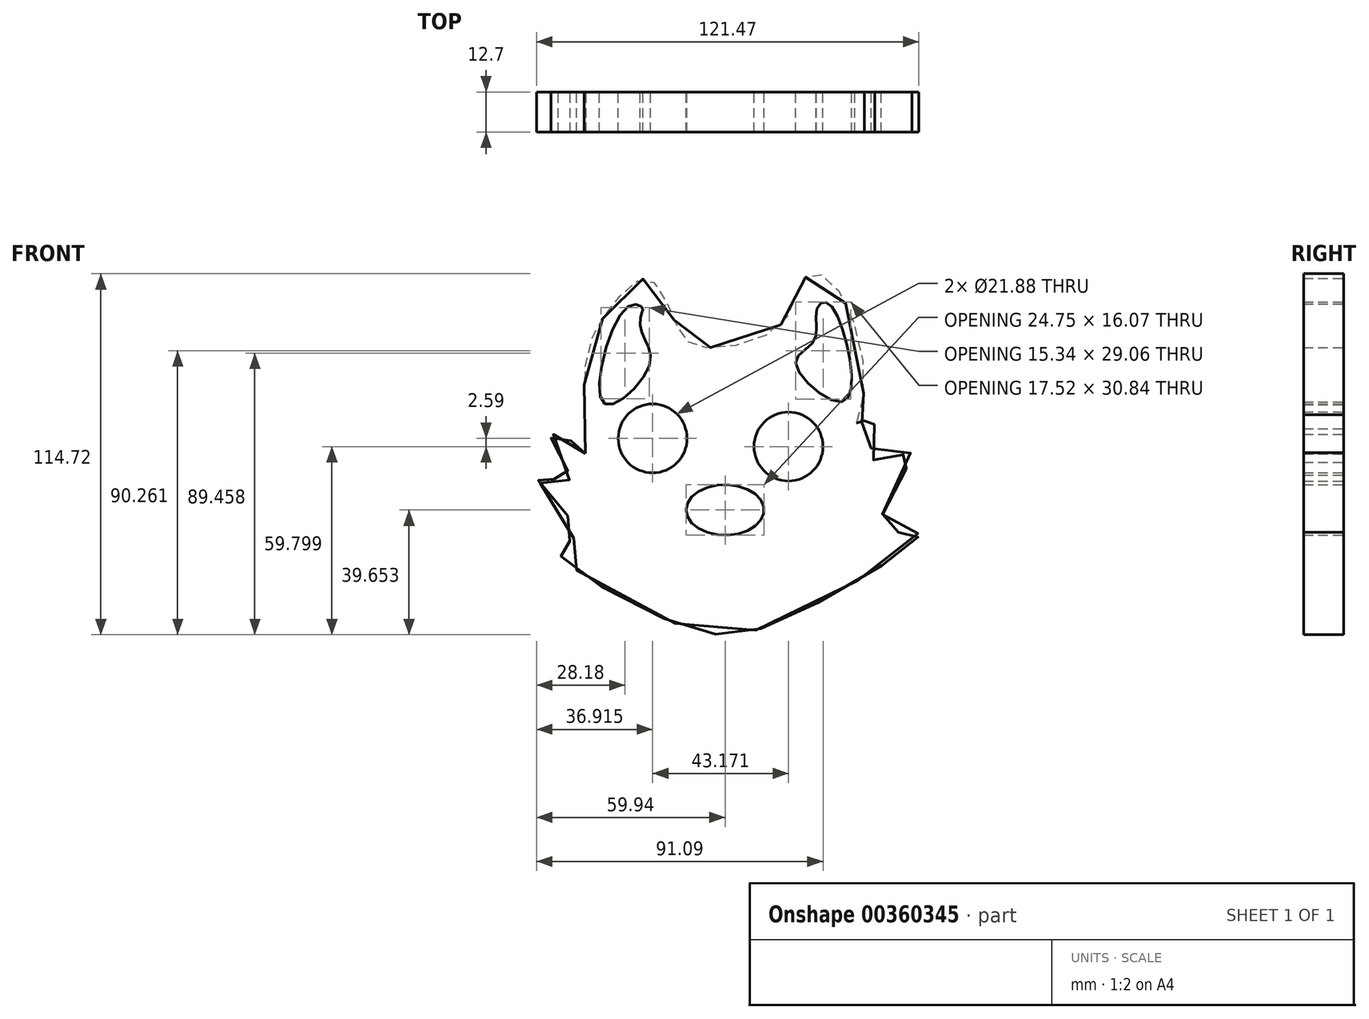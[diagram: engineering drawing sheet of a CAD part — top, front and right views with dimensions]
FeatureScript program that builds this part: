
annotation { "Feature Type Name" : "Feature", "Feature Type Description" : "" }
export const myFeature = defineFeature(function(context is Context, id is Id, definition is map)
    precondition{}
    {
        {
            var Q0;
            Q0=qCreatedBy(makeId("Front.planeOp"),FACE);
            var sketch = newSketch(context, id + "F0", { "sketchPlane" : qUnion([Q0])});
            skPoint(sketch, "E0", {"position": v(-44.4, 11.02) * mm});
            skPoint(sketch, "E1", {"position": v(-44.4, 38.57) * mm});
            skPoint(sketch, "E2", {"position": v(-35.98, 57.85) * mm});
            skPoint(sketch, "E3", {"position": v(-24.46, 66.48) * mm});
            skPoint(sketch, "E4", {"position": v(-15.54, 52.1) * mm});
            skFitSpline(sketch, "E5", {"points": [v(-44.4, 11.02) * mm, v(-44.4, 38.57) * mm, v(-35.98, 57.85) * mm, v(-24.46, 66.48) * mm, v(-15.54, 52.1) * mm, v(-8.15, 45.01) * mm, v(17.84, 52.1) * mm, v(25.04, 66.48) * mm, v(32.8, 66.48) * mm, v(44.03, 30.5) * mm, v(41.59, 19.05) * mm, v(47.2, 23.31) * mm, v(47.49, 8.63) * mm, v(59.29, 11.02) * mm, v(49.8, -12.09) * mm, v(61.3, -14.4) * mm, v(21.02, -40.63) * mm, v(-15.54, -43.02) * mm, v(-52.96, -19) * mm, v(-47.2, -14.4) * mm, v(-59.86, 4.03) * mm, v(-49.5, 2.6) * mm, v(-55.26, 16.4) * mm, v(-47.2, 13.81) * mm, v(-44.4, 11.02) * mm]});
            skCircle(sketch, "E6", {"center": v(20.15, 13.24) * mm, "radius": 10.94 * mm});
            skEllipse(sketch, "E7", {"center": v(0, -6.9) * mm, "majorRadius": 12.38 * mm, "minorRadius": 8.03 * mm, "majorAxis": v(-1, 0)});
            skFitSpline(sketch, "E8", {"points": [v(-24.1, 38.89) * mm, v(-26.48, 49.5) * mm, v(-26.48, 55.55) * mm, v(-26.2, 57.27) * mm, v(-31.08, 57.56) * mm, v(-38.57, 27.05) * mm, v(-24.1, 38.89) * mm]});
            skFitSpline(sketch, "E9", {"points": [v(22.39, 39.89) * mm, v(28.2, 46.62) * mm, v(29.07, 56.7) * mm, v(32.23, 59) * mm, v(39.72, 40.3) * mm, v(36.64, 27.39) * mm, v(22.39, 39.89) * mm]});
            skLineSegment(sketch, "E10", {"start": v(0, -14.94) * mm, "end": v(0, -27.63) * mm});
            skPoint(sketch, "E10.endSnap0", {"position": v(0, -14.94) * mm});
            skPoint(sketch, "E11", {"position": v(0, -27.63) * mm});
            skPoint(sketch, "E12", {"position": v(-11.8, -29.93) * mm});
            skPoint(sketch, "E13", {"position": v(-20.43, -21.3) * mm});
            skPoint(sketch, "E14", {"position": v(16.12, -21.87) * mm});
            skPoint(sketch, "E15", {"position": v(11.8, -32.23) * mm});
            skLineSegment(sketch, "E16", {"start": v(-24.46, -32.23) * mm, "end": v(-20.43, -27.63) * mm});
            skLineSegment(sketch, "E17", {"start": v(-20.43, -27.63) * mm, "end": v(-11.8, -40.63) * mm});
            skLineSegment(sketch, "E18", {"start": v(-11.8, -40.63) * mm, "end": v(0, -27.63) * mm});
            skLineSegment(sketch, "E19", {"start": v(0, -27.63) * mm, "end": v(11.8, -40.63) * mm});
            skLineSegment(sketch, "E20", {"start": v(11.8, -40.63) * mm, "end": v(18.7, -29.93) * mm});
            skLineSegment(sketch, "E21", {"start": v(23.89, -32.23) * mm, "end": v(18.7, -29.93) * mm});
            skCircle(sketch, "E22", {"center": v(-23.02, 15.83) * mm, "radius": 10.94 * mm});
            skSolve(sketch);
        }
        {
            var Q0;
            {var subQ0=sQuery(id+"F0.wireOp",EDGE,"E5");var subQ1=sQuery(id+"F0.wireOp",EDGE,"v4SeKJOA-A7Ss-Yav9-KnFC-fF1g7yY14pvq");var subQ2=makeQuery(id+"F0.imprint","INTERSECT",VERTEX,{"disambiguationData":[OD(0.0)],"derivedFrom":[subQ1,subQ0]});Q0=makeQuery(id+"F0.imprint","IMPRINT",FACE,{"disambiguationData":[TD([[makeQuery(id+"F0.imprint","IMPRINT",EDGE,{"disambiguationData":[TD([[subQ2,1.0]])],"derivedFrom":subQ1}),1.0]])]});}
            var Q1;
            {var subQ0=sQuery(id+"F0.wireOp",EDGE,"E5");var subQ1=sQuery(id+"F0.wireOp",EDGE,"v4SeKJOA-A7Ss-Yav9-KnFC-fF1g7yY14pvq");var subQ2=makeQuery(id+"F0.imprint","INTERSECT",VERTEX,{"disambiguationData":[OD(2.0)],"derivedFrom":[subQ1,subQ0]});Q1=makeQuery(id+"F0.imprint","IMPRINT",FACE,{"disambiguationData":[TD([[makeQuery(id+"F0.imprint","IMPRINT",EDGE,{"disambiguationData":[TD([[subQ2,-1.0]])],"derivedFrom":subQ1}),1.0]])]});}
            var Q2;
            {var subQ0=sQuery(id+"F0.wireOp",EDGE,"E5");var subQ1=sQuery(id+"F0.wireOp",EDGE,"v4SeKJOA-A7Ss-Yav9-KnFC-fF1g7yY14pvq");var subQ2=makeQuery(id+"F0.imprint","INTERSECT",VERTEX,{"disambiguationData":[OD(4.0)],"derivedFrom":[subQ1,subQ0]});Q2=makeQuery(id+"F0.imprint","IMPRINT",FACE,{"disambiguationData":[TD([[makeQuery(id+"F0.imprint","IMPRINT",EDGE,{"disambiguationData":[TD([[subQ2,-1.0]])],"derivedFrom":subQ1}),1.0]])]});}
            var Q3;
            {var subQ0=sQuery(id+"F0.wireOp",EDGE,"E5");var subQ1=sQuery(id+"F0.wireOp",EDGE,"v4SeKJOA-A7Ss-Yav9-KnFC-fF1g7yY14pvq");var subQ2=makeQuery(id+"F0.imprint","INTERSECT",VERTEX,{"disambiguationData":[OD(5.0)],"derivedFrom":[subQ1,subQ0]});Q3=makeQuery(id+"F0.imprint","IMPRINT",FACE,{"disambiguationData":[TD([[makeQuery(id+"F0.imprint","IMPRINT",EDGE,{"disambiguationData":[TD([[subQ2,-1.0]])],"derivedFrom":subQ1}),-1.0]])]});}
            var Q4;
            {var subQ0=sQuery(id+"F0.wireOp",EDGE,"E5");var subQ1=sQuery(id+"F0.wireOp",EDGE,"v4SeKJOA-A7Ss-Yav9-KnFC-fF1g7yY14pvq");var subQ2=makeQuery(id+"F0.imprint","INTERSECT",VERTEX,{"disambiguationData":[OD(6.0)],"derivedFrom":[subQ1,subQ0]});Q4=makeQuery(id+"F0.imprint","IMPRINT",FACE,{"disambiguationData":[TD([[makeQuery(id+"F0.imprint","IMPRINT",EDGE,{"disambiguationData":[TD([[subQ2,-1.0]])],"derivedFrom":subQ1}),1.0]])]});}
            var Q5;
            {var subQ0=sQuery(id+"F0.wireOp",EDGE,"E5");var subQ1=sQuery(id+"F0.wireOp",EDGE,"v4SeKJOA-A7Ss-Yav9-KnFC-fF1g7yY14pvq");var subQ2=makeQuery(id+"F0.imprint","INTERSECT",VERTEX,{"disambiguationData":[OD(7.0)],"derivedFrom":[subQ1,subQ0]});Q5=makeQuery(id+"F0.imprint","IMPRINT",FACE,{"disambiguationData":[TD([[makeQuery(id+"F0.imprint","IMPRINT",EDGE,{"disambiguationData":[TD([[subQ2,-1.0]])],"derivedFrom":subQ1}),-1.0]])]});}
            var Q6;
            {var subQ0=sQuery(id+"F0.wireOp",EDGE,"E5");var subQ1=sQuery(id+"F0.wireOp",EDGE,"v4SeKJOA-A7Ss-Yav9-KnFC-fF1g7yY14pvq");var subQ2=makeQuery(id+"F0.imprint","INTERSECT",VERTEX,{"disambiguationData":[OD(8.0)],"derivedFrom":[subQ1,subQ0]});Q6=makeQuery(id+"F0.imprint","IMPRINT",FACE,{"disambiguationData":[TD([[makeQuery(id+"F0.imprint","IMPRINT",EDGE,{"disambiguationData":[TD([[subQ2,-1.0]])],"derivedFrom":subQ1}),1.0]])]});}
            var Q7;
            {var subQ0=sQuery(id+"F0.wireOp",EDGE,"E5");var subQ1=sQuery(id+"F0.wireOp",EDGE,"v4SeKJOA-A7Ss-Yav9-KnFC-fF1g7yY14pvq");var subQ2=makeQuery(id+"F0.imprint","INTERSECT",VERTEX,{"disambiguationData":[OD(1.0)],"derivedFrom":[subQ1,subQ0]});Q7=makeQuery(id+"F0.imprint","IMPRINT",FACE,{"disambiguationData":[TD([[makeQuery(id+"F0.imprint","IMPRINT",EDGE,{"disambiguationData":[TD([[subQ2,1.0]])],"derivedFrom":subQ1}),-1.0]])]});}
            var Q8;
            {var subQ0=sQuery(id+"F0.wireOp",EDGE,"E5");var subQ1=sQuery(id+"F0.wireOp",EDGE,"v4SeKJOA-A7Ss-Yav9-KnFC-fF1g7yY14pvq");var subQ2=makeQuery(id+"F0.imprint","INTERSECT",VERTEX,{"disambiguationData":[OD(0.0)],"derivedFrom":[subQ1,subQ0]});Q8=makeQuery(id+"F0.imprint","IMPRINT",FACE,{"disambiguationData":[TD([[makeQuery(id+"F0.imprint","IMPRINT",EDGE,{"disambiguationData":[TD([[subQ2,-1.0]])],"derivedFrom":subQ1}),-1.0]])]});}
            var Q9;
            {var subQ0=sQuery(id+"F0.wireOp",EDGE,"E5");var subQ1=sQuery(id+"F0.wireOp",EDGE,"v4SeKJOA-A7Ss-Yav9-KnFC-fF1g7yY14pvq");var subQ2=makeQuery(id+"F0.imprint","INTERSECT",VERTEX,{"disambiguationData":[OD(3.0)],"derivedFrom":[subQ1,subQ0]});Q9=makeQuery(id+"F0.imprint","IMPRINT",FACE,{"disambiguationData":[TD([[makeQuery(id+"F0.imprint","IMPRINT",EDGE,{"disambiguationData":[TD([[subQ2,-1.0]])],"derivedFrom":subQ1}),-1.0]])]});}
            var Q10;
            Q10=makeQuery(id+"F0.imprint","IMPRINT",FACE,{"disambiguationData":[TD([[makeQuery(id+"F0.imprint","IMPRINT",EDGE,{"derivedFrom":sQuery(id+"F0.wireOp",EDGE,"E6")}),-1.0]])]});
            var Q11;
            {var subQ0=sQuery(id+"F0.wireOp",EDGE,"E5");var subQ1=sQuery(id+"F0.wireOp",EDGE,"v4SeKJOA-A7Ss-Yav9-KnFC-fF1g7yY14pvq");var subQ2=makeQuery(id+"F0.imprint","INTERSECT",VERTEX,{"disambiguationData":[OD(2.0)],"derivedFrom":[subQ1,subQ0]});Q11=makeQuery(id+"FG6cK2f71u9RmBc_0.opExtrude","CAP_FACE",FACE,{"disambiguationData":[OSD([subQ1,subQ0]),TDD([makeQuery(id+"F0.imprint","IMPRINT",EDGE,{"disambiguationData":[TD([[subQ2,-1.0]])],"derivedFrom":subQ1}),makeQuery(id+"F0.imprint","IMPRINT",EDGE,{"disambiguationData":[TD([[subQ2,1.0]])],"derivedFrom":subQ0})])],"isStart":false});}
            var Q12;
            Q12=makeQuery(id+"FG6cK2f71u9RmBc_0.opExtrude","CAP_FACE",FACE,{"disambiguationData":[OSD([sQuery(id+"F0.wireOp",EDGE,"v4SeKJOA-A7Ss-Yav9-KnFC-fF1g7yY14pvq"),sQuery(id+"F0.wireOp",EDGE,"E5"),sQuery(id+"F0.wireOp",EDGE,"E9")])],"isStart":true});
            var Q13;
            {var subQ0=sQuery(id+"F0.wireOp",EDGE,"E5");var subQ1=sQuery(id+"F0.wireOp",EDGE,"v4SeKJOA-A7Ss-Yav9-KnFC-fF1g7yY14pvq");var subQ2=makeQuery(id+"F0.imprint","INTERSECT",VERTEX,{"disambiguationData":[OD(2.0)],"derivedFrom":[subQ1,subQ0]});Q13=makeQuery(id+"FG6cK2f71u9RmBc_0.opExtrude","CAP_FACE",FACE,{"disambiguationData":[OSD([subQ1,subQ0]),TDD([makeQuery(id+"F0.imprint","IMPRINT",EDGE,{"disambiguationData":[TD([[subQ2,-1.0]])],"derivedFrom":subQ1}),makeQuery(id+"F0.imprint","IMPRINT",EDGE,{"disambiguationData":[TD([[subQ2,1.0]])],"derivedFrom":subQ0})])],"isStart":true});}
            var Q14;
            {var subQ0=sQuery(id+"F0.wireOp",EDGE,"E5");var subQ1=sQuery(id+"F0.wireOp",EDGE,"v4SeKJOA-A7Ss-Yav9-KnFC-fF1g7yY14pvq");var subQ2=makeQuery(id+"F0.imprint","INTERSECT",VERTEX,{"disambiguationData":[OD(0.0)],"derivedFrom":[subQ1,subQ0]});Q14=makeQuery(id+"FG6cK2f71u9RmBc_0.opExtrude","CAP_FACE",FACE,{"disambiguationData":[OSD([subQ1,subQ0]),TDD([makeQuery(id+"F0.imprint","IMPRINT",EDGE,{"disambiguationData":[TD([[subQ2,1.0]])],"derivedFrom":subQ1}),makeQuery(id+"F0.imprint","IMPRINT",EDGE,{"disambiguationData":[TD([[subQ2,-1.0]])],"derivedFrom":subQ0})])],"isStart":true});}
            extrude(context, id + "F1", {"entities" : qUnion([Q0, Q1, Q2, Q3, Q4, Q5, Q6, Q7, Q8, Q9, Q10, Q11, Q12, Q13, Q14]), "depth" : 12.7 * mm});
        }
        {
            var Q0;
            Q0=makeQuery(id+"F1.opExtrude","SWEPT_BODY",BODY,{"disambiguationData":[OSD([sQuery(id+"F0.wireOp",EDGE,"v4SeKJOA-A7Ss-Yav9-KnFC-fF1g7yY14pvq"),sQuery(id+"F0.wireOp",EDGE,"E5"),sQuery(id+"F0.wireOp",EDGE,"E6"),sQuery(id+"F0.wireOp",EDGE,"E7"),sQuery(id+"F0.wireOp",EDGE,"E8"),sQuery(id+"F0.wireOp",EDGE,"E9"),sQuery(id+"F0.wireOp",EDGE,"cbd609c7-798e-4a28-b2df-0b23a800b81f"),sQuery(id+"F0.wireOp",EDGE,"E17"),sQuery(id+"F0.wireOp",EDGE,"E20"),sQuery(id+"F0.wireOp",EDGE,"E22")])]});
            deleteBodies(context, id + "F2", {"entities" : qUnion([Q0])});
        }
        {
            var Q0;
            Q0 = qSketchRegion(id + "F0", true);
            extrude(context, id + "F3", {"entities" : qUnion([Q0]), "depth" : 12.7 * mm});
        }
    });
